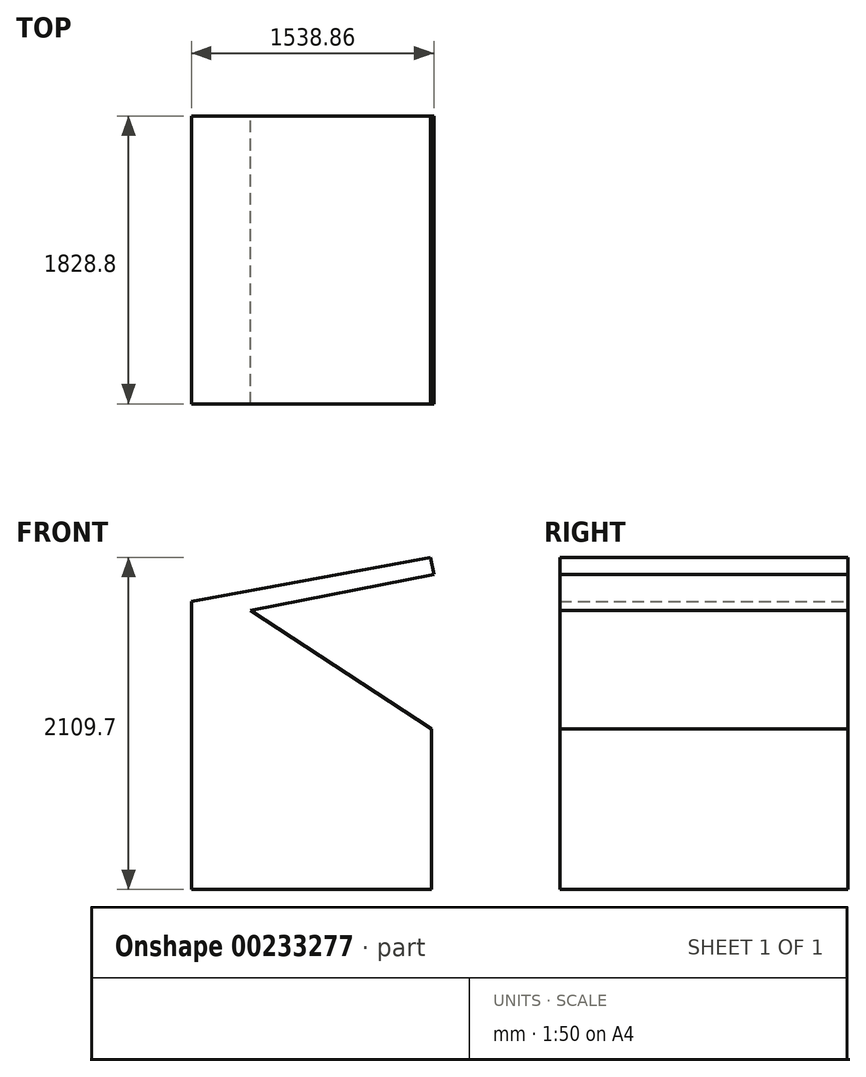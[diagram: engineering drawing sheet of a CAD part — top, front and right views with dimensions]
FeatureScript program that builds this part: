
annotation { "Feature Type Name" : "Feature", "Feature Type Description" : "" }
export const myFeature = defineFeature(function(context is Context, id is Id, definition is map)
    precondition{}
    {
        {
            var Q0;
            Q0=qCreatedBy(makeId("Front.planeOp"),FACE);
            var sketch = newSketch(context, id + "F0", { "sketchPlane" : qUnion([Q0])});
            skLineSegment(sketch, "E0.top", {"start": v(-63.26, -45.75) * mm, "end": v(1460.74, -45.75) * mm});
            skLineSegment(sketch, "E0.left", {"start": v(-63.26, 0) * mm, "end": v(-63.26, -45.75) * mm});
            skLineSegment(sketch, "E0.right", {"start": v(1460.74, 974.36) * mm, "end": v(1460.74, -45.75) * mm});
            skLineSegment(sketch, "E1", {"start": v(-62.98, 1783.05) * mm, "end": v(-63.26, 0) * mm});
            skLineSegment(sketch, "E2", {"start": v(-62.98, 1783.05) * mm, "end": v(1454.26, 2063.95) * mm});
            skLineSegment(sketch, "E3", {"start": v(1454.26, 2063.95) * mm, "end": v(1475.6, 1954.93) * mm});
            skLineSegment(sketch, "E4", {"start": v(1475.6, 1954.93) * mm, "end": v(311.79, 1727.12) * mm});
            skLineSegment(sketch, "E5", {"start": v(311.79, 1727.12) * mm, "end": v(1460.74, 974.36) * mm});
            skSolve(sketch);
        }
        {
            var Q0;
            Q0 = qSketchRegion(id + "F0", true);
            extrude(context, id + "F1", {"entities" : qUnion([Q0]), "depth" : 1828.8 * mm});
        }
    });
